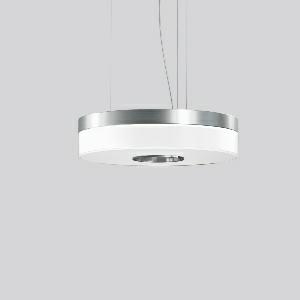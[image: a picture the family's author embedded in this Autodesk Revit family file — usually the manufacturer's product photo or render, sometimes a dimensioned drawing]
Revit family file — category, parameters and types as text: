
# Revit family: douala_312259_000_4c33
name_source: partatom
category: Lighting Fixtures
units: mm (PartAtom-declared; Revit-internal decimal feet)

## family parameters
Cut with Voids When Loaded = No
Host = Face
Light Source = No
Part Type = Normal
Room Calculation Point = No
Round Connector Dimension = Use Diameter
Shared = No

## types (1)
- DOUALA (1 x LED Modul 830, 2300 lm, 3000)
    Apparent Load = 24 VA
    CIE Flux Codes = 40 70 89 83 100
    Color Rendering = 80
    Color Temperature = 3000
    Default Elevation = 1800 mm
    Description = Series: DOUALA
Decorative round LED pendant luminaire. Base: brushed stainless steel. Mouth-blown, 3-layer opal glass, satin finish. With decorative screen, aluminium. Patented spring fastening system. Suitable for pendant. 3-point steel cable suspension, steplessly adjustable. Special lengths available on request. 
Colour: brushed stainless steel
Diameter: 400 mm
Height: 102 mm
Suspension length: 500-1200 mm
Lamp: LED exchangeable
Socket: without socket
Colour temperature: 3000K
Colour rendering index (CRI): 83
System power: 24 W
Rated luminous flux: 2300 lm
Luminous efficiency: 96 lm/W
Control gear: AC Strom, dim.Ph.an-/abschnitt
Protection class: I
Type of protection: IP 40
    Height = 102 mm
    Lamp = 1 x LED Modul 830
    Lamp Light Flux = 2300 lm
    Lamp count = 1
    Length = 400 mm
    Lifetime = 50000 h
    Luminous efficacy = 96 lm/W
    Manufacturer = RZB
    ModVariant = No
    Model = 312259.000
    Mounting Place = Ceiling
    Mounting Type = Pendant
    Number of Poles = 1
    OnlyDefault = Yes
    Power Factor = 1
    Product Name = DOUALA
    Product group = Pendant luminaires
    ProductGroupID = 902
    Protection Class = Protection class I
    Protection Degree = IP 40
    RLX_Detail_Level = 1
    RLX_Emergency_Light_Flux = 0 lm
    RLX_Emergency_Type = 0
    RLX_Emergency_Type_DB = No
    RlxData = <blob elided: 20345 chars, md5=7f456d8d>
    Socket = socket
    Standby Power = 0 W
    System Light Flux = 2300 lm
    System Power = 24 W
    Type Comments = Product without accessories
    Type Image = 311521.000.jpg
    URL = http://relux.com
    VarID = ---
    Voltage = 230 V
    Voltage Range = 220-240 V
    Weight = 0.00 kg
    Width = 0 mm  [stored 0 ft]

note: [stored X ft] marks values corroborated as IEEE doubles in the binary element streams (Revit-internal decimal feet)

## geometry (parser evidence)
native form markers: Blend x4, Sweep x11
no freeform markers — native parametric forms only
